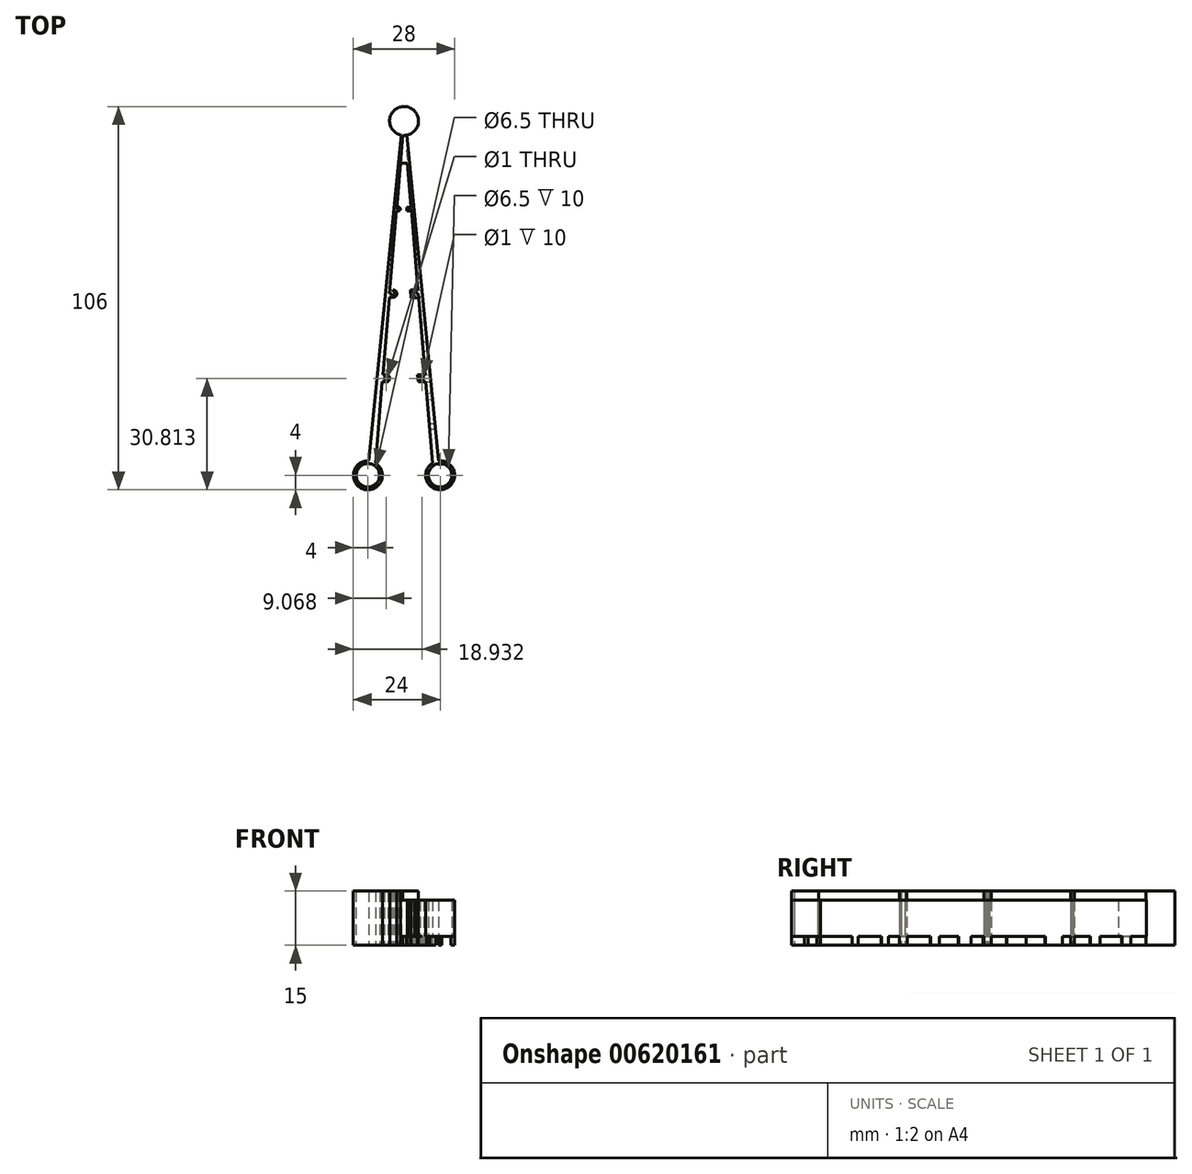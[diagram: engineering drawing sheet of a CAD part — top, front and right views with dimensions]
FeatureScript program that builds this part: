
annotation { "Feature Type Name" : "Feature", "Feature Type Description" : "" }
export const myFeature = defineFeature(function(context is Context, id is Id, definition is map)
    precondition{}
    {
        {
            var Q0;
            Q0=qCreatedBy(makeId("Top.planeOp"),FACE);
            var sketch = newSketch(context, id + "F0", { "sketchPlane" : qUnion([Q0])});
            skLineSegment(sketch, "E0", {"start": v(10.78, 94.08) * mm, "end": v(19.6, 3.98) * mm});
            skLineSegment(sketch, "E1", {"start": v(2.14, 23.44) * mm, "end": v(4.6, 48.04) * mm});
            skLineSegment(sketch, "E2", {"start": v(4.6, 48.04) * mm, "end": v(7.1, 73.04) * mm});
            skCircle(sketch, "E3", {"center": v(0, 0) * mm, "radius": 3.25 * mm});
            skCircle(sketch, "E4", {"center": v(0, 0) * mm, "radius": 4 * mm});
            skCircle(sketch, "E5", {"center": v(20, 0) * mm, "radius": 3.25 * mm});
            skCircle(sketch, "E6", {"center": v(20, 0) * mm, "radius": 4 * mm});
            skPoint(sketch, "E7.orphan", {"position": v(6.1, 23.04) * mm});
            skPoint(sketch, "E8.center.orphan", {"position": v(4.1, 23.04) * mm});
            skLineSegment(sketch, "E9", {"start": v(10.17, 96) * mm, "end": v(17.88, 3.4) * mm});
            skPoint(sketch, "E10.orphan", {"position": v(2.1, 23.04) * mm});
            skLineSegment(sketch, "E11.trimOffspring", {"start": v(2.12, 3.4) * mm, "end": v(9.83, 96) * mm});
            skLineSegment(sketch, "E12.trimOffspring", {"start": v(0.2, 4) * mm, "end": v(4.6, 48.04) * mm});
            skLineSegment(sketch, "E13", {"start": v(2.12, 3.4) * mm, "end": v(4.07, 26.81) * mm});
            skLineSegment(sketch, "E14", {"start": v(4.07, 26.81) * mm, "end": v(6.02, 50.23) * mm});
            skLineSegment(sketch, "E15", {"start": v(6.03, 50.4) * mm, "end": v(7.97, 73.65) * mm});
            skLineSegment(sketch, "E16", {"start": v(7.97, 73.65) * mm, "end": v(8.97, 73.65) * mm});
            skLineSegment(sketch, "E17", {"start": v(6.02, 50.23) * mm, "end": v(8.02, 50.23) * mm});
            skArc(sketch, "E18", {"start": v(5.07, 25.81) * mm, "mid": v(6.07, 26.81) * mm, "end": v(5.07, 27.81) * mm});
            skCircle(sketch, "E19", {"center": v(5.07, 26.81) * mm, "radius": 0.5 * mm});
            skArc(sketch, "E20", {"start": v(14.93, 27.81) * mm, "mid": v(13.93, 26.81) * mm, "end": v(14.93, 25.81) * mm});
            skCircle(sketch, "E21", {"center": v(14.93, 26.81) * mm, "radius": 0.5 * mm});
            skLineSegment(sketch, "E22", {"start": v(5.07, 27.81) * mm, "end": v(4.15, 27.81) * mm});
            skLineSegment(sketch, "E23", {"start": v(4.15, 27.81) * mm, "end": v(5.07, 27.81) * mm});
            skLineSegment(sketch, "E24", {"start": v(14.93, 26.31) * mm, "end": v(14.93, 25.81) * mm});
            skLineSegment(sketch, "E25", {"start": v(14.93, 25.81) * mm, "end": v(16.02, 25.81) * mm});
            skLineSegment(sketch, "E26", {"start": v(5.07, 25.81) * mm, "end": v(3.98, 25.81) * mm});
            skLineSegment(sketch, "E27.trimOffspring", {"start": v(14.93, 27.81) * mm, "end": v(15.85, 27.81) * mm});
            skPoint(sketch, "E28.orphan", {"position": v(6.07, 26.81) * mm});
            skPoint(sketch, "E29.trimOffspring.start.orphan", {"position": v(13.93, 26.81) * mm});
            skPoint(sketch, "E30.trimOffspring.end.orphan", {"position": v(15.93, 26.81) * mm});
            skLineSegment(sketch, "E31.trimOffspring", {"start": v(7.1, 73.04) * mm, "end": v(9.2, 94.08) * mm});
            skCircle(sketch, "E32", {"center": v(7.02, 50.23) * mm, "radius": 0.5 * mm});
            skArc(sketch, "E33", {"start": v(7.02, 49.23) * mm, "mid": v(8.02, 50.23) * mm, "end": v(7.02, 51.23) * mm});
            skLineSegment(sketch, "E34", {"start": v(13.98, 50.23) * mm, "end": v(11.98, 50.23) * mm});
            skArc(sketch, "E35", {"start": v(12.98, 51.23) * mm, "mid": v(11.98, 50.23) * mm, "end": v(12.98, 49.23) * mm});
            skCircle(sketch, "E36", {"center": v(12.98, 50.23) * mm, "radius": 0.5 * mm});
            skLineSegment(sketch, "E37", {"start": v(7.02, 50.23) * mm, "end": v(7.02, 51.23) * mm});
            skLineSegment(sketch, "E38", {"start": v(7.02, 51.23) * mm, "end": v(6.1, 51.23) * mm});
            skLineSegment(sketch, "E39", {"start": v(6.1, 51.23) * mm, "end": v(7.02, 51.23) * mm});
            skLineSegment(sketch, "E40", {"start": v(12.98, 50.23) * mm, "end": v(12.98, 49.23) * mm});
            skLineSegment(sketch, "E41", {"start": v(12.98, 49.23) * mm, "end": v(14.06, 49.23) * mm});
            skLineSegment(sketch, "E42", {"start": v(14.06, 49.23) * mm, "end": v(12.98, 49.23) * mm});
            skLineSegment(sketch, "E43.trimOffspring", {"start": v(12.98, 51.23) * mm, "end": v(13.9, 51.23) * mm});
            skLineSegment(sketch, "E44.trimOffspring", {"start": v(11.98, 50.23) * mm, "end": v(13.98, 50.23) * mm});
            skLineSegment(sketch, "E45.trimOffspring", {"start": v(7.02, 49.23) * mm, "end": v(5.94, 49.23) * mm});
            skLineSegment(sketch, "E46", {"start": v(12.03, 73.65) * mm, "end": v(11.03, 73.65) * mm});
            skArc(sketch, "E47", {"start": v(8.47, 73.15) * mm, "mid": v(8.97, 73.65) * mm, "end": v(8.47, 74.15) * mm});
            skArc(sketch, "E48", {"start": v(11.53, 74.15) * mm, "mid": v(11.03, 73.65) * mm, "end": v(11.53, 73.15) * mm});
            skCircle(sketch, "E49", {"center": v(8.47, 73.65) * mm, "radius": 0.25 * mm});
            skCircle(sketch, "E50", {"center": v(11.53, 73.65) * mm, "radius": 0.25 * mm});
            skLineSegment(sketch, "E51", {"start": v(8.47, 73.65) * mm, "end": v(8.47, 74.15) * mm});
            skLineSegment(sketch, "E52", {"start": v(8.47, 74.15) * mm, "end": v(8.01, 74.15) * mm});
            skLineSegment(sketch, "E53", {"start": v(8.01, 74.15) * mm, "end": v(8.47, 74.15) * mm});
            skLineSegment(sketch, "E54", {"start": v(11.53, 73.65) * mm, "end": v(11.53, 73.15) * mm});
            skLineSegment(sketch, "E55", {"start": v(11.53, 73.15) * mm, "end": v(12.07, 73.15) * mm});
            skLineSegment(sketch, "E56", {"start": v(12.07, 73.15) * mm, "end": v(11.53, 73.15) * mm});
            skLineSegment(sketch, "E57.trimOffspring", {"start": v(11.53, 74.15) * mm, "end": v(11.99, 74.15) * mm});
            skLineSegment(sketch, "E58.trimOffspring", {"start": v(11.03, 73.65) * mm, "end": v(12.03, 73.65) * mm});
            skLineSegment(sketch, "E59.trimOffspring", {"start": v(8.47, 73.15) * mm, "end": v(7.93, 73.15) * mm});
            skLineSegment(sketch, "E60", {"start": v(10.17, 96) * mm, "end": v(9.83, 96) * mm});
            skPoint(sketch, "E61.orphan", {"position": v(10, 98) * mm});
            skCircle(sketch, "E62", {"center": v(10, 98) * mm, "radius": 4 * mm});
            skPoint(sketch, "E63.orphan", {"position": v(10, 102) * mm});
            skLineSegment(sketch, "E64", {"start": v(10.97, 86.36) * mm, "end": v(9.03, 86.36) * mm});
            skSolve(sketch);
        }
        {
            var Q0;
            {var subQ0=sQuery(id+"F0.wireOp",EDGE,"E60");Q0=makeQuery(id+"F0.imprint","IMPRINT",FACE,{"disambiguationData":[TD([[makeQuery(id+"F0.imprint","IMPRINT",EDGE,{"derivedFrom":subQ0}),1.0]])]});}
            var Q1;
            Q1=makeQuery(id+"F0.imprint","IMPRINT",FACE,{"disambiguationData":[TD([[makeQuery(id+"F0.imprint","IMPRINT",EDGE,{"derivedFrom":sQuery(id+"F0.wireOp",EDGE,"E3")}),-1.0]])]});
            var Q2;
            Q2=makeQuery(id+"F0.imprint","IMPRINT",FACE,{"disambiguationData":[TD([[makeQuery(id+"F0.imprint","IMPRINT",EDGE,{"derivedFrom":sQuery(id+"F0.wireOp",EDGE,"E18")}),1.0]])]});
            var Q3;
            {var subQ0=sQuery(id+"F0.wireOp",EDGE,"E33");var subQ1=sQuery(id+"F0.wireOp",EDGE,"E17");var subQ2=makeQuery(id+"F0.imprint","INTERSECT",VERTEX,{"derivedFrom":[subQ1,subQ0]});Q3=makeQuery(id+"F0.imprint","IMPRINT",FACE,{"disambiguationData":[TD([[makeQuery(id+"F0.imprint","IMPRINT",EDGE,{"disambiguationData":[TD([[subQ2,1.0]])],"derivedFrom":subQ1}),1.0]])]});}
            var Q4;
            {var subQ0=sQuery(id+"F0.wireOp",EDGE,"E47");var subQ1=sQuery(id+"F0.wireOp",EDGE,"E16");var subQ2=makeQuery(id+"F0.imprint","INTERSECT",VERTEX,{"derivedFrom":[subQ1,subQ0]});Q4=makeQuery(id+"F0.imprint","IMPRINT",FACE,{"disambiguationData":[TD([[makeQuery(id+"F0.imprint","IMPRINT",EDGE,{"disambiguationData":[TD([[subQ2,1.0]])],"derivedFrom":subQ1}),1.0]])]});}
            var Q5;
            {var subQ0=sQuery(id+"F0.wireOp",EDGE,"E60");Q5=makeQuery(id+"F0.imprint","IMPRINT",FACE,{"disambiguationData":[TD([[makeQuery(id+"F0.imprint","IMPRINT",EDGE,{"derivedFrom":subQ0}),-1.0]])]});}
            var Q6;
            {var subQ5=sQuery(id+"F0.wireOp",EDGE,"E39");Q6=makeQuery(id+"F0.imprint","IMPRINT",FACE,{"disambiguationData":[TD([[makeQuery(id+"F0.imprint","IMPRINT",EDGE,{"derivedFrom":subQ5}),-1.0]])]});}
            var Q7;
            {var subQ0=sQuery(id+"F0.wireOp",EDGE,"E53");Q7=makeQuery(id+"F0.imprint","IMPRINT",FACE,{"disambiguationData":[TD([[makeQuery(id+"F0.imprint","IMPRINT",EDGE,{"derivedFrom":subQ0}),-1.0]])]});}
            var Q8;
            {var subQ6=sQuery(id+"F0.wireOp",EDGE,"E45.trimOffspring");Q8=makeQuery(id+"F0.imprint","IMPRINT",FACE,{"disambiguationData":[TD([[makeQuery(id+"F0.imprint","IMPRINT",EDGE,{"derivedFrom":subQ6}),-1.0]])]});}
            var Q9;
            {var subQ5=sQuery(id+"F0.wireOp",EDGE,"E59.trimOffspring");Q9=makeQuery(id+"F0.imprint","IMPRINT",FACE,{"disambiguationData":[TD([[makeQuery(id+"F0.imprint","IMPRINT",EDGE,{"derivedFrom":subQ5}),-1.0]])]});}
            var Q10;
            {var subQ3=sQuery(id+"F0.wireOp",EDGE,"E2");Q10=makeQuery(id+"F0.imprint","IMPRINT",FACE,{"disambiguationData":[TD([[makeQuery(id+"F0.imprint","IMPRINT",EDGE,{"derivedFrom":subQ3}),-1.0]])]});}
            extrude(context, id + "F1", {"entities" : qUnion([Q0, Q1, Q2, Q3, Q4, Q5, Q6, Q7, Q8, Q9, Q10]), "depth" : 15 * mm, "offsetDistance" : 25 * mm});
        }
        {
            var Q0;
            {var subQ8=sQuery(id+"F0.wireOp",EDGE,"E0");Q0=makeQuery(id+"F0.imprint","IMPRINT",FACE,{"disambiguationData":[TD([[makeQuery(id+"F0.imprint","IMPRINT",EDGE,{"derivedFrom":subQ8}),-1.0]])]});}
            var Q1;
            Q1=makeQuery(id+"F0.imprint","IMPRINT",FACE,{"disambiguationData":[TD([[makeQuery(id+"F0.imprint","IMPRINT",EDGE,{"derivedFrom":sQuery(id+"F0.wireOp",EDGE,"E5")}),-1.0]])]});
            var Q2;
            Q2=makeQuery(id+"F0.imprint","IMPRINT",FACE,{"disambiguationData":[TD([[makeQuery(id+"F0.imprint","IMPRINT",EDGE,{"derivedFrom":sQuery(id+"F0.wireOp",EDGE,"E20")}),1.0]])]});
            var Q3;
            {var subQ3=sQuery(id+"F0.wireOp",EDGE,"E44.trimOffspring");var subQ5=sQuery(id+"F0.wireOp",EDGE,"E36");var subQ6=makeQuery(id+"F0.imprint","INTERSECT",VERTEX,{"disambiguationData":[OD(0.0)],"derivedFrom":[subQ5,subQ3]});Q3=makeQuery(id+"F0.imprint","IMPRINT",FACE,{"disambiguationData":[TD([[makeQuery(id+"F0.imprint","IMPRINT",EDGE,{"disambiguationData":[TD([[subQ6,-1.0]])],"derivedFrom":subQ5}),-1.0]])]});}
            var Q4;
            {var subQ0=sQuery(id+"F0.wireOp",EDGE,"E42");Q4=makeQuery(id+"F0.imprint","IMPRINT",FACE,{"disambiguationData":[TD([[makeQuery(id+"F0.imprint","IMPRINT",EDGE,{"derivedFrom":subQ0}),-1.0]])]});}
            var Q5;
            {var subQ0=sQuery(id+"F0.wireOp",EDGE,"E43.trimOffspring");Q5=makeQuery(id+"F0.imprint","IMPRINT",FACE,{"disambiguationData":[TD([[makeQuery(id+"F0.imprint","IMPRINT",EDGE,{"derivedFrom":subQ0}),-1.0]])]});}
            var Q6;
            {var subQ0=sQuery(id+"F0.wireOp",EDGE,"E56");Q6=makeQuery(id+"F0.imprint","IMPRINT",FACE,{"disambiguationData":[TD([[makeQuery(id+"F0.imprint","IMPRINT",EDGE,{"derivedFrom":subQ0}),-1.0]])]});}
            var Q7;
            {var subQ3=sQuery(id+"F0.wireOp",EDGE,"E58.trimOffspring");var subQ5=sQuery(id+"F0.wireOp",EDGE,"E50");var subQ6=makeQuery(id+"F0.imprint","INTERSECT",VERTEX,{"disambiguationData":[OD(0.0)],"derivedFrom":[subQ5,subQ3]});Q7=makeQuery(id+"F0.imprint","IMPRINT",FACE,{"disambiguationData":[TD([[makeQuery(id+"F0.imprint","IMPRINT",EDGE,{"disambiguationData":[TD([[subQ6,-1.0]])],"derivedFrom":subQ5}),-1.0]])]});}
            var Q8;
            {var subQ4=sQuery(id+"F0.wireOp",EDGE,"E57.trimOffspring");Q8=makeQuery(id+"F0.imprint","IMPRINT",FACE,{"disambiguationData":[TD([[makeQuery(id+"F0.imprint","IMPRINT",EDGE,{"derivedFrom":subQ4}),-1.0]])]});}
            extrude(context, id + "F2", {"entities" : qUnion([Q0, Q1, Q2, Q3, Q4, Q5, Q6, Q7, Q8]), "operationType" : NewBodyOperationType.ADD, "depth" : 12.5 * mm, "offsetDistance" : 25 * mm});
        }
        {
            var Q0;
            {var subQ8=sQuery(id+"F0.wireOp",EDGE,"E0");Q0=makeQuery(id+"F0.imprint","IMPRINT",FACE,{"disambiguationData":[TD([[makeQuery(id+"F0.imprint","IMPRINT",EDGE,{"derivedFrom":subQ8}),-1.0]])]});}
            var Q1;
            Q1=makeQuery(id+"F0.imprint","IMPRINT",FACE,{"disambiguationData":[TD([[makeQuery(id+"F0.imprint","IMPRINT",EDGE,{"derivedFrom":sQuery(id+"F0.wireOp",EDGE,"E5")}),-1.0]])]});
            var Q2;
            Q2=makeQuery(id+"F0.imprint","IMPRINT",FACE,{"disambiguationData":[TD([[makeQuery(id+"F0.imprint","IMPRINT",EDGE,{"derivedFrom":sQuery(id+"F0.wireOp",EDGE,"E20")}),1.0]])]});
            var Q3;
            {var subQ0=sQuery(id+"F0.wireOp",EDGE,"E43.trimOffspring");Q3=makeQuery(id+"F0.imprint","IMPRINT",FACE,{"disambiguationData":[TD([[makeQuery(id+"F0.imprint","IMPRINT",EDGE,{"derivedFrom":subQ0}),-1.0]])]});}
            var Q4;
            {var subQ0=sQuery(id+"F0.wireOp",EDGE,"E42");Q4=makeQuery(id+"F0.imprint","IMPRINT",FACE,{"disambiguationData":[TD([[makeQuery(id+"F0.imprint","IMPRINT",EDGE,{"derivedFrom":subQ0}),-1.0]])]});}
            var Q5;
            {var subQ3=sQuery(id+"F0.wireOp",EDGE,"E44.trimOffspring");var subQ5=sQuery(id+"F0.wireOp",EDGE,"E36");var subQ6=makeQuery(id+"F0.imprint","INTERSECT",VERTEX,{"disambiguationData":[OD(0.0)],"derivedFrom":[subQ5,subQ3]});Q5=makeQuery(id+"F0.imprint","IMPRINT",FACE,{"disambiguationData":[TD([[makeQuery(id+"F0.imprint","IMPRINT",EDGE,{"disambiguationData":[TD([[subQ6,-1.0]])],"derivedFrom":subQ5}),-1.0]])]});}
            var Q6;
            {var subQ4=sQuery(id+"F0.wireOp",EDGE,"E57.trimOffspring");Q6=makeQuery(id+"F0.imprint","IMPRINT",FACE,{"disambiguationData":[TD([[makeQuery(id+"F0.imprint","IMPRINT",EDGE,{"derivedFrom":subQ4}),-1.0]])]});}
            var Q7;
            {var subQ0=sQuery(id+"F0.wireOp",EDGE,"E56");Q7=makeQuery(id+"F0.imprint","IMPRINT",FACE,{"disambiguationData":[TD([[makeQuery(id+"F0.imprint","IMPRINT",EDGE,{"derivedFrom":subQ0}),-1.0]])]});}
            var Q8;
            {var subQ3=sQuery(id+"F0.wireOp",EDGE,"E58.trimOffspring");var subQ5=sQuery(id+"F0.wireOp",EDGE,"E50");var subQ6=makeQuery(id+"F0.imprint","INTERSECT",VERTEX,{"disambiguationData":[OD(0.0)],"derivedFrom":[subQ5,subQ3]});Q8=makeQuery(id+"F0.imprint","IMPRINT",FACE,{"disambiguationData":[TD([[makeQuery(id+"F0.imprint","IMPRINT",EDGE,{"disambiguationData":[TD([[subQ6,-1.0]])],"derivedFrom":subQ5}),-1.0]])]});}
            extrude(context, id + "F3", {"entities" : qUnion([Q0, Q1, Q2, Q3, Q4, Q5, Q6, Q7, Q8]), "operationType" : NewBodyOperationType.REMOVE, "depth" : 2.5 * mm, "offsetDistance" : 25 * mm});
        }
        {
            var Q0;
            Q0=qCreatedBy(makeId("Top.planeOp"),FACE);
            var sketch = newSketch(context, id + "F4", { "sketchPlane" : qUnion([Q0])});
            skLineSegment(sketch, "E65", {"start": v(0, 0) * mm, "end": v(20, 0) * mm});
            skLineSegment(sketch, "E66", {"start": v(20, 0) * mm, "end": v(20, -4) * mm});
            skLineSegment(sketch, "E67", {"start": v(20, -4) * mm, "end": v(16, -4) * mm});
            skLineSegment(sketch, "E68", {"start": v(16, -4) * mm, "end": v(16, 4) * mm});
            skLineSegment(sketch, "E69", {"start": v(16, 4) * mm, "end": v(24, 4) * mm});
            skLineSegment(sketch, "E70", {"start": v(24, 4) * mm, "end": v(24, -4) * mm});
            skLineSegment(sketch, "E71", {"start": v(24, -4) * mm, "end": v(20, -4) * mm});
            skCircle(sketch, "E72", {"center": v(20, 0) * mm, "radius": 4 * mm});
            skLineSegment(sketch, "E73", {"start": v(20, -4) * mm, "end": v(20, -3) * mm});
            skCircle(sketch, "E74", {"center": v(20, -3.5) * mm, "radius": 0.5 * mm});
            skLineSegment(sketch, "E75", {"start": v(16, 0) * mm, "end": v(17, 0) * mm});
            skCircle(sketch, "E76", {"center": v(16.5, 0) * mm, "radius": 0.5 * mm});
            skLineSegment(sketch, "E77", {"start": v(24, 0) * mm, "end": v(23, 0) * mm});
            skPoint(sketch, "E77.endSnap0", {"position": v(24, 0) * mm});
            skCircle(sketch, "E78", {"center": v(23.5, 0) * mm, "radius": 0.5 * mm});
            skLineSegment(sketch, "E79", {"start": v(20, 4) * mm, "end": v(20, 3) * mm});
            skCircle(sketch, "E80", {"center": v(20, 3.5) * mm, "radius": 0.5 * mm});
            skLineSegment(sketch, "E81.0", {"start": v(10.78, 94.08) * mm, "end": v(19.6, 3.98) * mm});
            skLineSegment(sketch, "E82.0", {"start": v(16.02, 25.81) * mm, "end": v(17.88, 3.4) * mm});
            skLineSegment(sketch, "E83.0", {"start": v(14.06, 49.23) * mm, "end": v(15.85, 27.81) * mm});
            skLineSegment(sketch, "E84.0", {"start": v(14.93, 27.81) * mm, "end": v(15.85, 27.81) * mm});
            skArc(sketch, "E85.0", {"start": v(14.93, 27.81) * mm, "mid": v(13.93, 26.81) * mm, "end": v(14.93, 25.81) * mm});
            skLineSegment(sketch, "E86.0", {"start": v(14.93, 25.81) * mm, "end": v(16.02, 25.81) * mm});
            skLineSegment(sketch, "E87.0", {"start": v(12.98, 51.23) * mm, "end": v(13.9, 51.23) * mm});
            skArc(sketch, "E88.0", {"start": v(12.98, 51.23) * mm, "mid": v(11.98, 50.23) * mm, "end": v(12.98, 49.23) * mm});
            skLineSegment(sketch, "E89.0", {"start": v(14.06, 49.23) * mm, "end": v(12.98, 49.23) * mm});
            skLineSegment(sketch, "E90.0", {"start": v(12.07, 73.15) * mm, "end": v(13.9, 51.23) * mm});
            skLineSegment(sketch, "E91.0", {"start": v(10.33, 94.01) * mm, "end": v(11.99, 74.15) * mm});
            skArc(sketch, "E92.0", {"start": v(11.53, 74.15) * mm, "mid": v(11.03, 73.65) * mm, "end": v(11.53, 73.15) * mm});
            skLineSegment(sketch, "E93.0", {"start": v(12.07, 73.15) * mm, "end": v(11.53, 73.15) * mm});
            skLineSegment(sketch, "E94.0", {"start": v(11.53, 74.15) * mm, "end": v(11.99, 74.15) * mm});
            skLineSegment(sketch, "E95", {"start": v(18.75, 12.73) * mm, "end": v(17.1, 12.73) * mm});
            skLineSegment(sketch, "E96", {"start": v(17.1, 12.73) * mm, "end": v(16.97, 14.35) * mm});
            skLineSegment(sketch, "E97", {"start": v(16.97, 14.35) * mm, "end": v(18.6, 14.35) * mm});
            skLineSegment(sketch, "E98", {"start": v(18.6, 14.35) * mm, "end": v(18.75, 12.73) * mm});
            skLineSegment(sketch, "E99", {"start": v(17.95, 20.9) * mm, "end": v(16.44, 20.78) * mm});
            skLineSegment(sketch, "E100", {"start": v(16.44, 20.78) * mm, "end": v(16.28, 22.63) * mm});
            skLineSegment(sketch, "E101", {"start": v(16.28, 22.63) * mm, "end": v(17.77, 22.77) * mm});
            skLineSegment(sketch, "E102", {"start": v(18.75, 12.73) * mm, "end": v(18.6, 14.35) * mm});
            skLineSegment(sketch, "E103", {"start": v(16.97, 14.35) * mm, "end": v(17.1, 12.73) * mm});
            skLineSegment(sketch, "E104", {"start": v(17.77, 22.77) * mm, "end": v(17.95, 20.9) * mm});
            skLineSegment(sketch, "E105", {"start": v(17.47, 25.81) * mm, "end": v(13.93, 25.81) * mm});
            skPoint(sketch, "E105.endSnap0", {"position": v(13.93, 26.81) * mm});
            skLineSegment(sketch, "E106", {"start": v(13.93, 25.81) * mm, "end": v(13.74, 27.81) * mm});
            skLineSegment(sketch, "E107", {"start": v(13.74, 27.81) * mm, "end": v(15.85, 27.81) * mm});
            skLineSegment(sketch, "E108", {"start": v(15.85, 27.81) * mm, "end": v(17.26, 27.95) * mm});
            skLineSegment(sketch, "E109", {"start": v(16.4, 36.82) * mm, "end": v(15.1, 36.82) * mm});
            skLineSegment(sketch, "E110", {"start": v(15.1, 36.82) * mm, "end": v(15.3, 34.37) * mm});
            skLineSegment(sketch, "E111", {"start": v(15.3, 34.37) * mm, "end": v(16.62, 34.5) * mm});
            skLineSegment(sketch, "E112", {"start": v(16.62, 34.5) * mm, "end": v(16.4, 36.82) * mm});
            skLineSegment(sketch, "E113", {"start": v(15.17, 49.23) * mm, "end": v(11.98, 48.97) * mm});
            skPoint(sketch, "E113.endSnap0", {"position": v(11.98, 50.23) * mm});
            skLineSegment(sketch, "E114", {"start": v(11.98, 48.97) * mm, "end": v(11.8, 51.23) * mm});
            skLineSegment(sketch, "E115", {"start": v(11.8, 51.23) * mm, "end": v(13.9, 51.23) * mm});
            skLineSegment(sketch, "E116", {"start": v(14.98, 51.23) * mm, "end": v(13.9, 51.23) * mm});
            skLineSegment(sketch, "E117", {"start": v(15.86, 42.2) * mm, "end": v(14.66, 42.08) * mm});
            skLineSegment(sketch, "E118", {"start": v(14.66, 42.08) * mm, "end": v(14.38, 45.49) * mm});
            skLineSegment(sketch, "E119", {"start": v(14.38, 45.49) * mm, "end": v(15.53, 45.6) * mm});
            skLineSegment(sketch, "E120", {"start": v(15.53, 45.6) * mm, "end": v(15.86, 42.2) * mm});
            skLineSegment(sketch, "E121", {"start": v(14.55, 55.55) * mm, "end": v(13.54, 55.46) * mm});
            skLineSegment(sketch, "E122", {"start": v(13.54, 55.46) * mm, "end": v(13.1, 60.82) * mm});
            skLineSegment(sketch, "E123", {"start": v(13.1, 60.82) * mm, "end": v(13.9, 60.9) * mm});
            skLineSegment(sketch, "E124", {"start": v(13.9, 60.9) * mm, "end": v(14.55, 55.55) * mm});
            skLineSegment(sketch, "E125", {"start": v(13.51, 66.19) * mm, "end": v(12.66, 66.11) * mm});
            skLineSegment(sketch, "E126", {"start": v(12.66, 66.11) * mm, "end": v(12.26, 70.87) * mm});
            skLineSegment(sketch, "E127", {"start": v(12.26, 70.87) * mm, "end": v(13.04, 70.94) * mm});
            skLineSegment(sketch, "E128", {"start": v(13.04, 70.94) * mm, "end": v(13.51, 66.19) * mm});
            skLineSegment(sketch, "E129", {"start": v(12.83, 73.15) * mm, "end": v(10.76, 73.15) * mm});
            skLineSegment(sketch, "E130", {"start": v(10.76, 73.15) * mm, "end": v(10.76, 74.15) * mm});
            skLineSegment(sketch, "E131", {"start": v(10.76, 74.15) * mm, "end": v(12.73, 74.15) * mm});
            skLineSegment(sketch, "E132", {"start": v(12.73, 74.15) * mm, "end": v(12.83, 73.15) * mm});
            skLineSegment(sketch, "E133", {"start": v(12.3, 78.61) * mm, "end": v(11.62, 78.56) * mm});
            skLineSegment(sketch, "E134", {"start": v(11.62, 78.56) * mm, "end": v(11.4, 81.24) * mm});
            skLineSegment(sketch, "E135", {"start": v(11.4, 81.24) * mm, "end": v(12.03, 81.3) * mm});
            skLineSegment(sketch, "E136", {"start": v(12.03, 81.3) * mm, "end": v(12.3, 78.61) * mm});
            skLineSegment(sketch, "E137", {"start": v(11.44, 87.34) * mm, "end": v(10.9, 87.3) * mm});
            skLineSegment(sketch, "E138", {"start": v(10.9, 87.3) * mm, "end": v(10.68, 89.83) * mm});
            skLineSegment(sketch, "E139", {"start": v(10.68, 89.83) * mm, "end": v(11.19, 89.88) * mm});
            skLineSegment(sketch, "E140", {"start": v(11.19, 89.88) * mm, "end": v(11.44, 87.34) * mm});
            skSolve(sketch);
        }
        {
            var Q0;
            {var subQ0=sQuery(id+"F4.wireOp",EDGE,"E73");Q0=makeQuery(id+"F4.imprint","IMPRINT",FACE,{"disambiguationData":[TD([[makeQuery(id+"F4.imprint","IMPRINT",EDGE,{"derivedFrom":subQ0}),-1.0]])]});}
            var Q1;
            {var subQ0=sQuery(id+"F4.wireOp",EDGE,"E73");Q1=makeQuery(id+"F4.imprint","IMPRINT",FACE,{"disambiguationData":[TD([[makeQuery(id+"F4.imprint","IMPRINT",EDGE,{"derivedFrom":subQ0}),1.0]])]});}
            var Q2;
            {var subQ0=sQuery(id+"F4.wireOp",EDGE,"E75");Q2=makeQuery(id+"F4.imprint","IMPRINT",FACE,{"disambiguationData":[TD([[makeQuery(id+"F4.imprint","IMPRINT",EDGE,{"derivedFrom":subQ0}),-1.0]])]});}
            var Q3;
            {var subQ0=sQuery(id+"F4.wireOp",EDGE,"E75");Q3=makeQuery(id+"F4.imprint","IMPRINT",FACE,{"disambiguationData":[TD([[makeQuery(id+"F4.imprint","IMPRINT",EDGE,{"derivedFrom":subQ0}),1.0]])]});}
            var Q4;
            {var subQ0=sQuery(id+"F4.wireOp",EDGE,"E79");Q4=makeQuery(id+"F4.imprint","IMPRINT",FACE,{"disambiguationData":[TD([[makeQuery(id+"F4.imprint","IMPRINT",EDGE,{"derivedFrom":subQ0}),1.0]])]});}
            var Q5;
            {var subQ0=sQuery(id+"F4.wireOp",EDGE,"E79");Q5=makeQuery(id+"F4.imprint","IMPRINT",FACE,{"disambiguationData":[TD([[makeQuery(id+"F4.imprint","IMPRINT",EDGE,{"derivedFrom":subQ0}),-1.0]])]});}
            var Q6;
            {var subQ0=sQuery(id+"F4.wireOp",EDGE,"E77");Q6=makeQuery(id+"F4.imprint","IMPRINT",FACE,{"disambiguationData":[TD([[makeQuery(id+"F4.imprint","IMPRINT",EDGE,{"derivedFrom":subQ0}),-1.0]])]});}
            var Q7;
            {var subQ0=sQuery(id+"F4.wireOp",EDGE,"E77");Q7=makeQuery(id+"F4.imprint","IMPRINT",FACE,{"disambiguationData":[TD([[makeQuery(id+"F4.imprint","IMPRINT",EDGE,{"derivedFrom":subQ0}),1.0]])]});}
            extrude(context, id + "F5", {"entities" : qUnion([Q0, Q1, Q2, Q3, Q4, Q5, Q6, Q7]), "operationType" : NewBodyOperationType.ADD, "depth" : 2.5 * mm, "offsetDistance" : 25 * mm});
        }
        {
            var Q0;
            Q0=makeQuery(id+"F4.imprint","IMPRINT",FACE,{"disambiguationData":[TD([[makeQuery(id+"F4.imprint","IMPRINT",EDGE,{"derivedFrom":sQuery(id+"F4.wireOp",EDGE,"E95")}),-1.0]])]});
            var Q1;
            Q1=makeQuery(id+"F4.imprint","IMPRINT",FACE,{"disambiguationData":[TD([[makeQuery(id+"F4.imprint","IMPRINT",EDGE,{"derivedFrom":sQuery(id+"F4.wireOp",EDGE,"E99")}),-1.0]])]});
            var Q2;
            {var subQ2=sQuery(id+"F4.wireOp",EDGE,"E85.0");Q2=makeQuery(id+"F4.imprint","IMPRINT",FACE,{"disambiguationData":[TD([[makeQuery(id+"F4.imprint","IMPRINT",EDGE,{"derivedFrom":subQ2}),1.0]])]});}
            var Q3;
            {var subQ0=sQuery(id+"F4.wireOp",EDGE,"E85.0");Q3=makeQuery(id+"F4.imprint","IMPRINT",FACE,{"disambiguationData":[TD([[makeQuery(id+"F4.imprint","IMPRINT",EDGE,{"derivedFrom":subQ0}),-1.0]])]});}
            var Q4;
            Q4=makeQuery(id+"F4.imprint","IMPRINT",FACE,{"disambiguationData":[TD([[makeQuery(id+"F4.imprint","IMPRINT",EDGE,{"derivedFrom":sQuery(id+"F4.wireOp",EDGE,"E109")}),1.0]])]});
            var Q5;
            Q5=makeQuery(id+"F4.imprint","IMPRINT",FACE,{"disambiguationData":[TD([[makeQuery(id+"F4.imprint","IMPRINT",EDGE,{"derivedFrom":sQuery(id+"F4.wireOp",EDGE,"E117")}),-1.0]])]});
            var Q6;
            {var subQ1=sQuery(id+"F4.wireOp",EDGE,"E88.0");Q6=makeQuery(id+"F4.imprint","IMPRINT",FACE,{"disambiguationData":[TD([[makeQuery(id+"F4.imprint","IMPRINT",EDGE,{"derivedFrom":subQ1}),1.0]])]});}
            var Q7;
            {var subQ5=sQuery(id+"F4.wireOp",EDGE,"E88.0");Q7=makeQuery(id+"F4.imprint","IMPRINT",FACE,{"disambiguationData":[TD([[makeQuery(id+"F4.imprint","IMPRINT",EDGE,{"derivedFrom":subQ5}),-1.0]])]});}
            var Q8;
            Q8=makeQuery(id+"F4.imprint","IMPRINT",FACE,{"disambiguationData":[TD([[makeQuery(id+"F4.imprint","IMPRINT",EDGE,{"derivedFrom":sQuery(id+"F4.wireOp",EDGE,"E121")}),-1.0]])]});
            var Q9;
            Q9=makeQuery(id+"F4.imprint","IMPRINT",FACE,{"disambiguationData":[TD([[makeQuery(id+"F4.imprint","IMPRINT",EDGE,{"derivedFrom":sQuery(id+"F4.wireOp",EDGE,"E125")}),-1.0]])]});
            var Q10;
            {var subQ2=sQuery(id+"F4.wireOp",EDGE,"E92.0");Q10=makeQuery(id+"F4.imprint","IMPRINT",FACE,{"disambiguationData":[TD([[makeQuery(id+"F4.imprint","IMPRINT",EDGE,{"derivedFrom":subQ2}),1.0]])]});}
            var Q11;
            {var subQ0=sQuery(id+"F4.wireOp",EDGE,"E92.0");Q11=makeQuery(id+"F4.imprint","IMPRINT",FACE,{"disambiguationData":[TD([[makeQuery(id+"F4.imprint","IMPRINT",EDGE,{"derivedFrom":subQ0}),-1.0]])]});}
            var Q12;
            Q12=makeQuery(id+"F4.imprint","IMPRINT",FACE,{"disambiguationData":[TD([[makeQuery(id+"F4.imprint","IMPRINT",EDGE,{"derivedFrom":sQuery(id+"F4.wireOp",EDGE,"E133")}),-1.0]])]});
            var Q13;
            Q13=makeQuery(id+"F4.imprint","IMPRINT",FACE,{"disambiguationData":[TD([[makeQuery(id+"F4.imprint","IMPRINT",EDGE,{"derivedFrom":sQuery(id+"F4.wireOp",EDGE,"E137")}),-1.0]])]});
            extrude(context, id + "F6", {"entities" : qUnion([Q0, Q1, Q2, Q3, Q4, Q5, Q6, Q7, Q8, Q9, Q10, Q11, Q12, Q13]), "operationType" : NewBodyOperationType.ADD, "depth" : 2.5 * mm, "offsetDistance" : 25 * mm});
        }
        {
            var Q0;
            {var subQ0=sQuery(id+"F0.wireOp",EDGE,"E64");Q0=makeQuery(id+"F0.imprint","IMPRINT",FACE,{"disambiguationData":[TD([[makeQuery(id+"F0.imprint","IMPRINT",EDGE,{"derivedFrom":subQ0}),-1.0]])]});}
            extrude(context, id + "F7", {"entities" : qUnion([Q0]), "operationType" : NewBodyOperationType.ADD, "depth" : 12.5 * mm, "offsetDistance" : 25 * mm});
        }
        {
            var Q0;
            {var subQ0=sQuery(id+"F0.wireOp",EDGE,"E64");Q0=makeQuery(id+"F0.imprint","IMPRINT",FACE,{"disambiguationData":[TD([[makeQuery(id+"F0.imprint","IMPRINT",EDGE,{"derivedFrom":subQ0}),-1.0]])]});}
            extrude(context, id + "F8", {"entities" : qUnion([Q0]), "operationType" : NewBodyOperationType.REMOVE, "depth" : 2.5 * mm, "offsetDistance" : 25 * mm});
        }
    });
